# Revit family: str-pc
name_source: partatom
category: Generic Models
revit_build: Autodesk Revit 2014 (Build: 20130308_1515(x64)
units: mm (PartAtom-declared; Revit-internal decimal feet)

## types (7) — shared parameters
1 = 3/4"

## per-type parameters (varying)
- STR2.00-IRON-FLG: 2L=1"; 2L2=4 1/2"; 3CUT=1/8"; 3H=4"; 3L=4"; 3R=1/4"; 3thk=1 1/2"; 4L=1 3/8"; 4h=6"; H=5 3/4"; Hole=1/8"; ID=1"; ID2=1/4"; L=9 1/8"; L1=5/8"; L2=3"; L3=1 1/2"; Material=Iron, Ductile; OD=2 1/4"; OD1=1 7/8"; PLUG=1/2"; R1=0"; R2=5 1/2"; R3=4"; RP1=1 3/4"; RP123=3/4"; SIZE=2"; od2=2 3/8"; plug L=3 3/8"; plugh=3 1/2"
- STR2.50-IRON-FLG: 2L=1 3/4"; 2L2=6"; 3CUT=1/4"; 3H=5 1/2"; 3L=5 1/2"; 3R=1/4"; 3thk=2"; 4L=2"; 4h=3"; H=6 7/8"; Hole=1/4"; ID=1 1/4"; ID2=3/8"; L=11 5/8"; L1=3/4"; L2=5 1/2"; L3=1 3/4"; Material=DUCTILE IRON; OD=2 1/2"; OD1=2 1/2"; PLUG=1/2"; R1=1/8"; R2=3"; R3=6"; RP1=1 3/4"; RP123=1"; SIZE=2 1/2"; od2=2 3/4"; plug L=3 3/8"; plugh=3 1/2"
- STR3.00-IRON-FLG: 2L=1 1/2"; 2L2=6 1/8"; 3CUT=1/4"; 3H=5 1/2"; 3L=5"; 3R=1/2"; 3thk=2"; 4L=1 1/2"; 4h=3 1/2"; H=7 3/4"; Hole=1/4"; ID=1 1/2"; ID2=3/8"; L=11 5/8"; L1=7/8"; L2=5 3/8"; L3=1/2"; Material=Iron, Ductile; OD=3"; OD1=2 1/4"; PLUG=1/2"; R1=1/8"; R2=4 1/2"; R3=8"; RP1=1 3/4"; RP123=1"; SIZE=3"; od2=3 1/4"; plug L=3 3/8"; plugh=3 1/2"
- STR4.00-IRON-FLG: 2L=3"; 2L2=7 1/8"; 3CUT=1/4"; 3H=7"; 3L=8"; 3R=2"; 3thk=2 1/2"; 4L=2"; 4h=3 1/2"; H=9 1/8"; Hole=1/2"; ID=2"; ID2=1/2"; L=13 7/8"; L1=1 1/8"; L2=6 1/2"; L3=1 1/2"; Material=Iron, Ductile; OD=4"; OD1=3"; PLUG=5/8"; R1=1/8"; R2=4 1/4"; R3=6"; RP1=1 1/8"; RP123=1 1/4"; SIZE=4"; od2=4 3/8"; plug L=3 7/8"; plugh=3 1/2"
- STR6.00-IRON-FLG: 2L=4 3/4"; 2L2=11"; 3CUT=1/2"; 3H=9"; 3L=9"; 3R=2"; 3thk=4"; 4L=2 1/2"; 4h=5"; H=12"; Hole=1/2"; ID=3"; ID2=3/4"; L=18 1/2"; L1=1 3/4"; L2=8"; L3=3 1/8"; Material=Iron, Ductile; OD=5"; OD1=4 1/4"; PLUG=1 1/2"; R1=1/4"; R2=6"; R3=5 1/4"; RP1=2 1/4"; RP123=2"; SIZE=6"; od2=6"; plug L=5 1/2"; plugh=2 1/2"
- STR8.00-IRON-FLG: 2L=7"; 2L2=12"; 3CUT=1/2"; 3H=11"; 3L=12"; 3R=2 1/2"; 3thk=4 1/2"; 4L=3"; 4h=6"; H=15 3/4"; Hole=5/8"; ID=4"; ID2=1"; L=21 3/8"; L1=2 1/4"; L2=10"; L3=1"; Material=Iron, Ductile; OD=6 1/2"; OD1=6"; PLUG=1 1/2"; R1=1/4"; R2=7"; R3=8"; RP1=1 3/4"; RP123=2 1/4"; SIZE=8"; od2=7 7/8"; plug L=3 3/8"; plugh=3 1/2"
- STR10.00-IRON-FLG: 2L=10"; 2L2=15"; 3CUT=1/2"; 3H=16"; 3L=16"; 3R=3"; 3thk=4 1/2"; 4L=4"; 4h=6"; H=17"; Hole=1"; ID=5"; ID2=1 1/4"; L=28 5/8"; L1=2 7/8"; L2=13"; L3=1 1/2"; Material=Iron, Ductile; OD=9"; OD1=7 1/2"; PLUG=1 1/2"; R1=1/4"; R2=9"; R3=16"; RP1=1 3/4"; RP123=2 1/4"; SIZE=10"; od2=10 1/4"; plug L=3 3/8"; plugh=3 1/2"

## geometry (parser evidence)
native form markers: Sweep x1
no freeform markers — native parametric forms only
